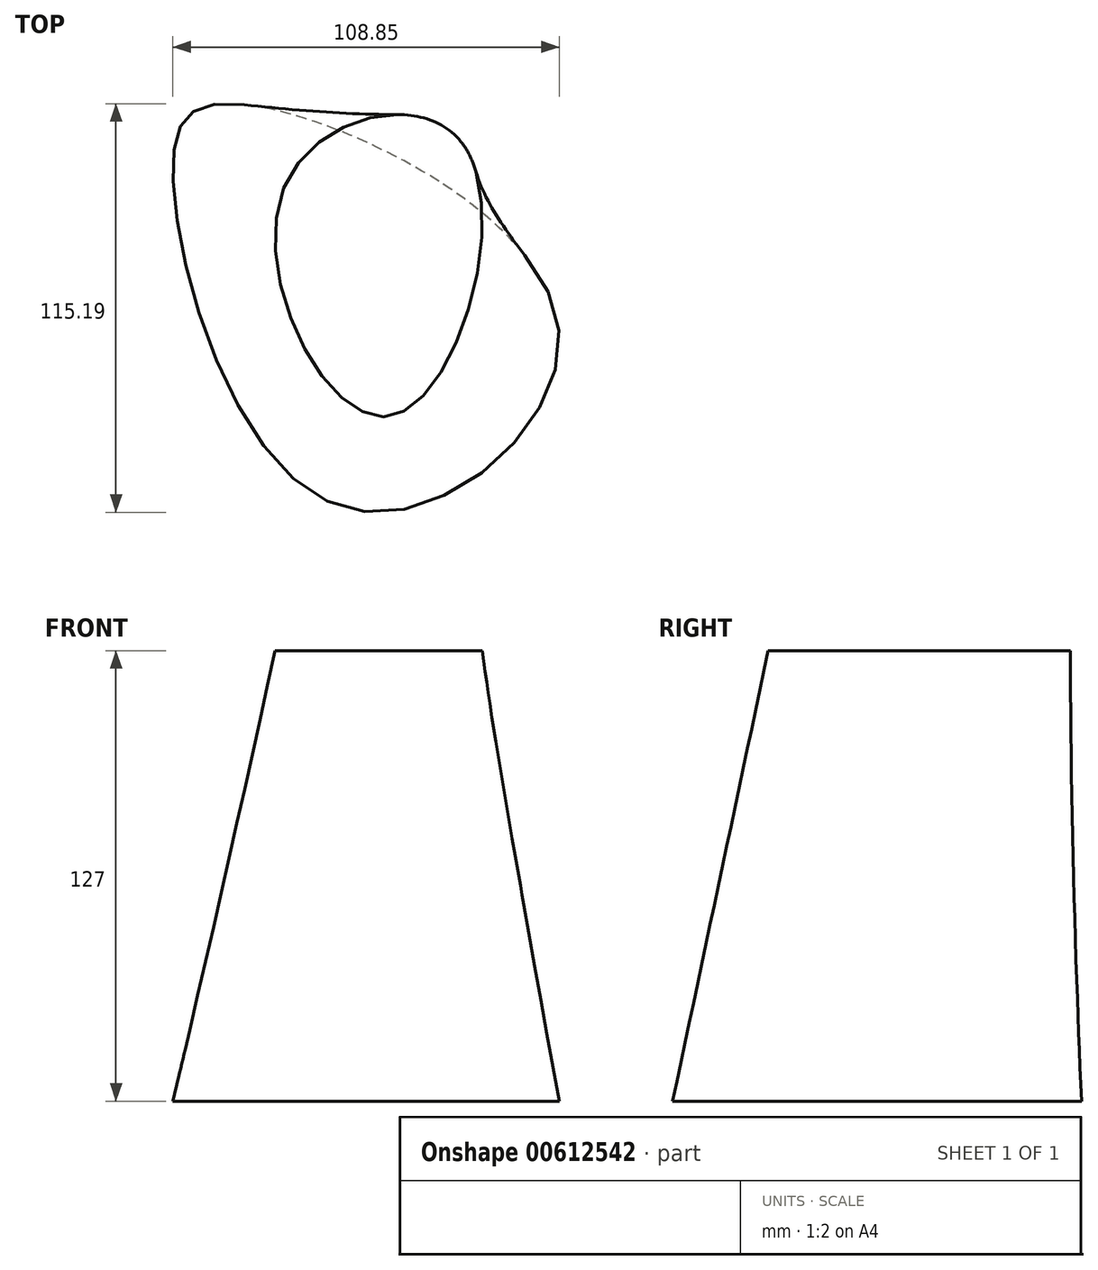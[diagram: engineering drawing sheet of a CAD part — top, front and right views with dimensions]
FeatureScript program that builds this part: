
annotation { "Feature Type Name" : "Feature", "Feature Type Description" : "" }
export const myFeature = defineFeature(function(context is Context, id is Id, definition is map)
    precondition{}
    {
        {
            var Q0;
            Q0=qCreatedBy(makeId("Top.planeOp"),FACE);
            var sketch = newSketch(context, id + "F0", { "sketchPlane" : qUnion([Q0])});
            skFitSpline(sketch, "E0", {"points": [v(-45, 62.32) * mm, v(-61.1, 43.37) * mm, v(-11.91, -51.89) * mm, v(47.44, 0) * mm, v(-45, 62.32) * mm]});
            skSolve(sketch);
        }
        {
            var Q0;
            Q0=qCreatedBy(makeId("Top.planeOp"),FACE);
            cPlane(context, id + "F1", {"entities" : qUnion([Q0]), "cplaneType" : CPlaneType.OFFSET, "offset" : 127 * mm, "width" : 152.4 * mm, "height" : 152.4 * mm});
        }
        {
            var Q0;
            Q0=qCreatedBy(id+"F1.planeOp",FACE);
            var sketch = newSketch(context, id + "F2", { "sketchPlane" : qUnion([Q0])});
            skFitSpline(sketch, "E1", {"points": [v(20.58, 50.92) * mm, v(-30, 38.14) * mm, v(0, -25.8) * mm, v(20.58, 50.92) * mm]});
            skSolve(sketch);
        }
        {
            var Q0;
            Q0=makeQuery(id+"F2.imprint","IMPRINT",FACE,{"disambiguationData":[TD([[makeQuery(id+"F2.imprint","IMPRINT",EDGE,{"derivedFrom":sQuery(id+"F2.wireOp",EDGE,"E1")}),1.0]])]});
            var Q1;
            Q1=makeQuery(id+"F0.imprint","IMPRINT",FACE,{"disambiguationData":[TD([[makeQuery(id+"F0.imprint","IMPRINT",EDGE,{"derivedFrom":sQuery(id+"F0.wireOp",EDGE,"E0")}),1.0]])]});
            loft(context, id + "F3", {"sheetProfilesArray" : [{ "sheetProfileEntities" : qUnion([Q0]) }, { "sheetProfileEntities" : qUnion([Q1]) }]});
        }
    });
